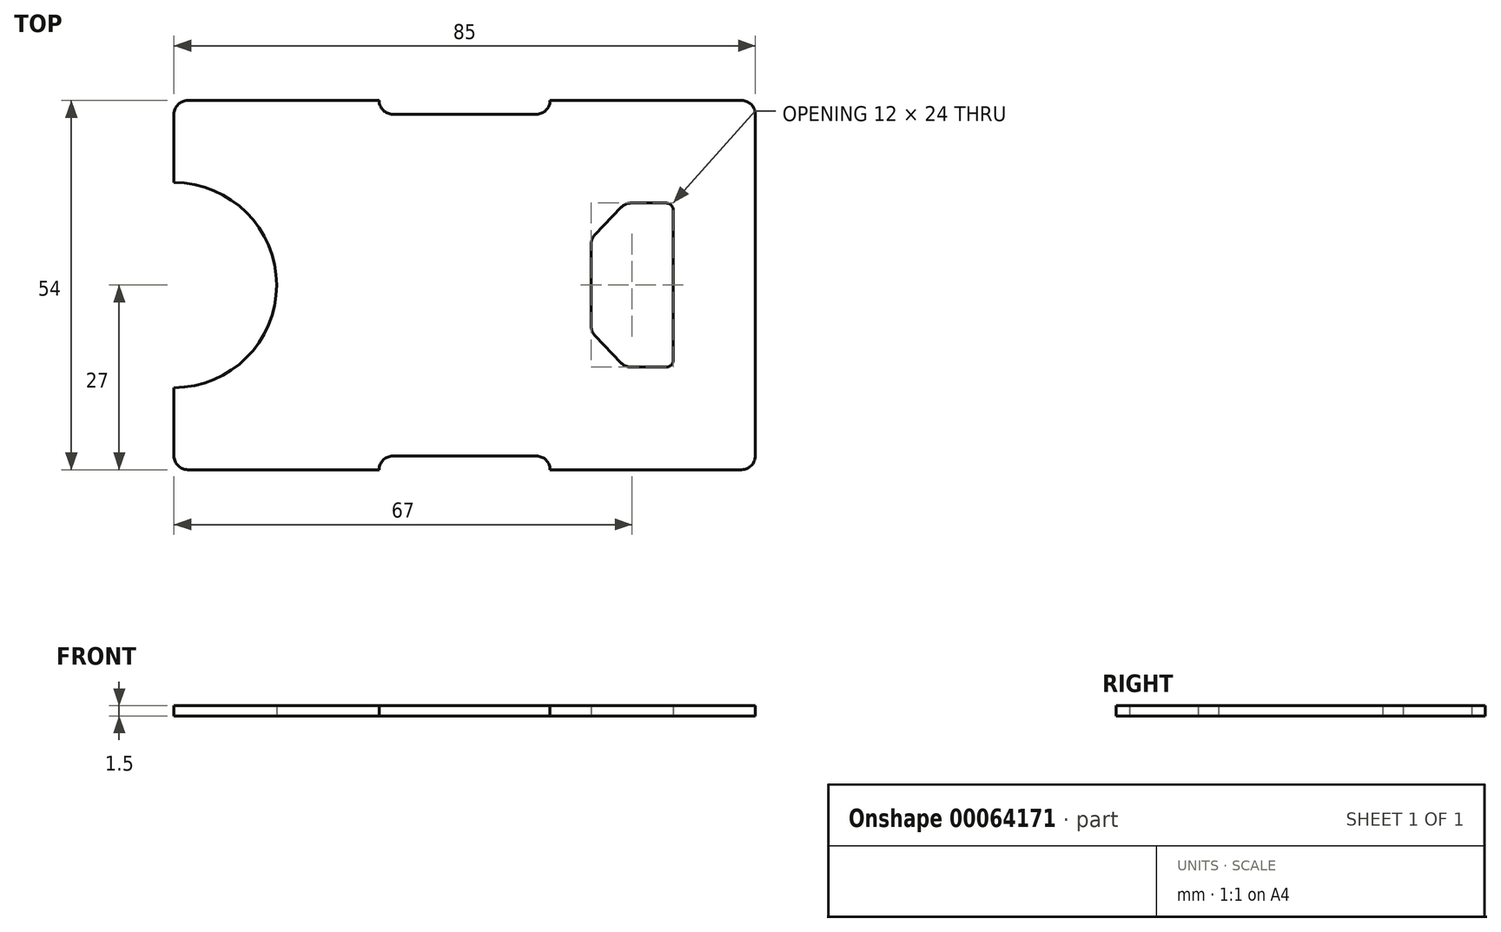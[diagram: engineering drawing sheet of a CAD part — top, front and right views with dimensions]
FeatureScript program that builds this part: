
annotation { "Feature Type Name" : "Feature", "Feature Type Description" : "" }
export const myFeature = defineFeature(function(context is Context, id is Id, definition is map)
    precondition{}
    {
        {
            var Q0;
            Q0=qCreatedBy(makeId("Top.planeOp"),FACE);
            var sketch = newSketch(context, id + "F0", { "sketchPlane" : qUnion([Q0])});
            skLineSegment(sketch, "E0.rect.bottom", {"start": v(40.5, -27) * mm, "end": v(-40.5, -27) * mm});
            skLineSegment(sketch, "E0.rect.top", {"start": v(40.5, 27) * mm, "end": v(-40.5, 27) * mm});
            skLineSegment(sketch, "E0.rect.left", {"start": v(42.5, -25) * mm, "end": v(42.5, 25) * mm});
            skLineSegment(sketch, "E0.rect.right", {"start": v(-42.5, -25) * mm, "end": v(-42.5, 25) * mm});
            skPoint(sketch, "E0.rect.middle", {"position": v(0, 0) * mm});
            skPoint(sketch, "E1.visualSharp", {"position": v(-42.5, 27) * mm});
            skArc(sketch, "E1.filletArc", {"start": v(-40.5, 27) * mm, "mid": v(-41.91, 26.41) * mm, "end": v(-42.5, 25) * mm});
            skPoint(sketch, "E2.visualSharp", {"position": v(-42.5, -27) * mm});
            skArc(sketch, "E2.filletArc", {"start": v(-42.5, -25) * mm, "mid": v(-41.91, -26.41) * mm, "end": v(-40.5, -27) * mm});
            skPoint(sketch, "E3.visualSharp", {"position": v(42.5, -27) * mm});
            skArc(sketch, "E3.filletArc", {"start": v(40.5, -27) * mm, "mid": v(41.91, -26.41) * mm, "end": v(42.5, -25) * mm});
            skPoint(sketch, "E4.visualSharp", {"position": v(42.5, 27) * mm});
            skArc(sketch, "E4.filletArc", {"start": v(42.5, 25) * mm, "mid": v(41.91, 26.41) * mm, "end": v(40.5, 27) * mm});
            skArc(sketch, "E5", {"start": v(-42.5, -15) * mm, "mid": v(-27.5, 0) * mm, "end": v(-42.5, 15) * mm});
            skLineSegment(sketch, "E6", {"start": v(30.5, 0) * mm, "end": v(30.5, -11) * mm});
            skLineSegment(sketch, "E7", {"start": v(29.5, -12) * mm, "end": v(24.35, -12) * mm});
            skLineSegment(sketch, "E8", {"start": v(22.9, -11.39) * mm, "end": v(19.06, -7.39) * mm});
            skLineSegment(sketch, "E9", {"start": v(18.5, -6) * mm, "end": v(18.5, 0) * mm});
            skLineSegment(sketch, "E10.MirrorCS", {"start": v(30.5, 0) * mm, "end": v(30.5, 11) * mm});
            skLineSegment(sketch, "E11.MirrorCS", {"start": v(29.5, 12) * mm, "end": v(24.35, 12) * mm});
            skLineSegment(sketch, "E12.MirrorCS", {"start": v(22.9, 11.39) * mm, "end": v(19.06, 7.39) * mm});
            skLineSegment(sketch, "E13.MirrorCS", {"start": v(18.5, 6) * mm, "end": v(18.5, 0) * mm});
            skPoint(sketch, "E14.visualSharp", {"position": v(18.5, -6.8) * mm});
            skArc(sketch, "E14.filletArc", {"start": v(18.5, -6) * mm, "mid": v(18.65, -6.75) * mm, "end": v(19.06, -7.39) * mm});
            skPoint(sketch, "E15.visualSharp", {"position": v(23.5, -12) * mm});
            skArc(sketch, "E15.filletArc", {"start": v(22.9, -11.39) * mm, "mid": v(23.57, -11.84) * mm, "end": v(24.35, -12) * mm});
            skPoint(sketch, "E16.visualSharp", {"position": v(30.5, -12) * mm});
            skArc(sketch, "E16.filletArc", {"start": v(29.5, -12) * mm, "mid": v(30.2, -11.7) * mm, "end": v(30.5, -11) * mm});
            skPoint(sketch, "E17.visualSharp", {"position": v(30.5, 12) * mm});
            skArc(sketch, "E17.filletArc", {"start": v(30.5, 11) * mm, "mid": v(30.2, 11.7) * mm, "end": v(29.5, 12) * mm});
            skPoint(sketch, "E18.visualSharp", {"position": v(23.5, 12) * mm});
            skArc(sketch, "E18.filletArc", {"start": v(24.35, 12) * mm, "mid": v(23.57, 11.84) * mm, "end": v(22.9, 11.39) * mm});
            skPoint(sketch, "E19.visualSharp", {"position": v(18.5, 6.8) * mm});
            skArc(sketch, "E19.filletArc", {"start": v(19.06, 7.39) * mm, "mid": v(18.65, 6.75) * mm, "end": v(18.5, 6) * mm});
            skLineSegment(sketch, "E20.rect.bottom", {"start": v(10.5, 25) * mm, "end": v(-10.5, 25) * mm});
            skPoint(sketch, "E20.rect.middle", {"position": v(0, 27) * mm});
            skLineSegment(sketch, "E21.rect.top", {"start": v(10.5, -25) * mm, "end": v(-10.5, -25) * mm});
            skPoint(sketch, "E21.rect.middle", {"position": v(0, -27) * mm});
            skPoint(sketch, "E22.orphan", {"position": v(-10.5, 29) * mm});
            skPoint(sketch, "E23.orphan", {"position": v(10.5, 29) * mm});
            skPoint(sketch, "E24.orphan", {"position": v(-10.5, -29) * mm});
            skPoint(sketch, "E25.orphan", {"position": v(10.5, -29) * mm});
            skArc(sketch, "E26", {"start": v(-12.5, 27) * mm, "mid": v(-11.91, 25.59) * mm, "end": v(-10.5, 25) * mm});
            skArc(sketch, "E27", {"start": v(10.5, 25) * mm, "mid": v(11.91, 25.59) * mm, "end": v(12.5, 27) * mm});
            skArc(sketch, "E28", {"start": v(-10.5, -25) * mm, "mid": v(-11.91, -25.59) * mm, "end": v(-12.5, -27) * mm});
            skArc(sketch, "E29", {"start": v(12.5, -27) * mm, "mid": v(11.91, -25.59) * mm, "end": v(10.5, -25) * mm});
            skSolve(sketch);
        }
        {
            var Q0;
            Q0=makeQuery(id+"F0.imprint","IMPRINT",FACE,{"disambiguationData":[TD([[makeQuery(id+"F0.imprint","IMPRINT",EDGE,{"derivedFrom":sQuery(id+"F0.wireOp",EDGE,"E0.rect.left")}),1.0]])]});
            extrude(context, id + "F1", {"entities" : qUnion([Q0]), "depth" : 1.5 * mm});
        }
    });
